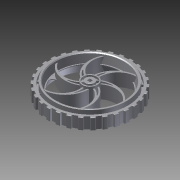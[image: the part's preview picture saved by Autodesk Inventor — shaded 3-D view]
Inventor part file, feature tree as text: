
AUTODESK INVENTOR PART (.ipt)
format: ipt  version: 2013 (Build 170138000, 138)  size: 1,378,304 bytes
history: native  units: mm (DEFAULTED — no unit token found)
features: imported_body x1, sketch x1, other x1, extrude x1
ambient origin geometry x8: Origin, YZ Plane, XZ Plane, XY Plane, X Axis, Y Axis, Z Axis, Center Point
bodies: Solid1 (feature_tree)
feature tree (4):
  imported_body  "Base1"
  sketch  "Sketch1"  dims[d0=25.4mm d1=0.0mm d2=0.0mm d3=0.0mm]
  other  "Srf1"
  extrude  "ExtrusionSrf1"  TaperAngle=0.0deg  [1 undecoded]
note: 1 required parameter value undecoded (feature->parameter linkage not recoverable at this tier; creation-order binding heuristic only, values carry confidence <= 0.55)
